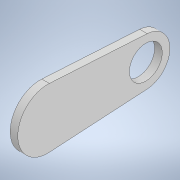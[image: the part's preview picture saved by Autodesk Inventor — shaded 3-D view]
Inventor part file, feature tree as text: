
AUTODESK INVENTOR PART (.ipt)
format: ipt  version: 2020 (Build 240168000, 168)  size: 143,360 bytes
history: native  units: mm
features: sketch x3, extrude x1, projected_geometry x1
ambient origin geometry x8: Origin, YZ Plane, XZ Plane, XY Plane, X Axis, Y Axis, Z Axis, Center Point
bodies: Body1 (feature_tree)
feature tree (5):
  extrude  "Выдавливание4"  Depth=18.6mm
  sketch  "Эскиз4"
  sketch  "Эскиз5"
  sketch  "Эскиз1"
  projected_geometry  "Спроецированная петля3"
